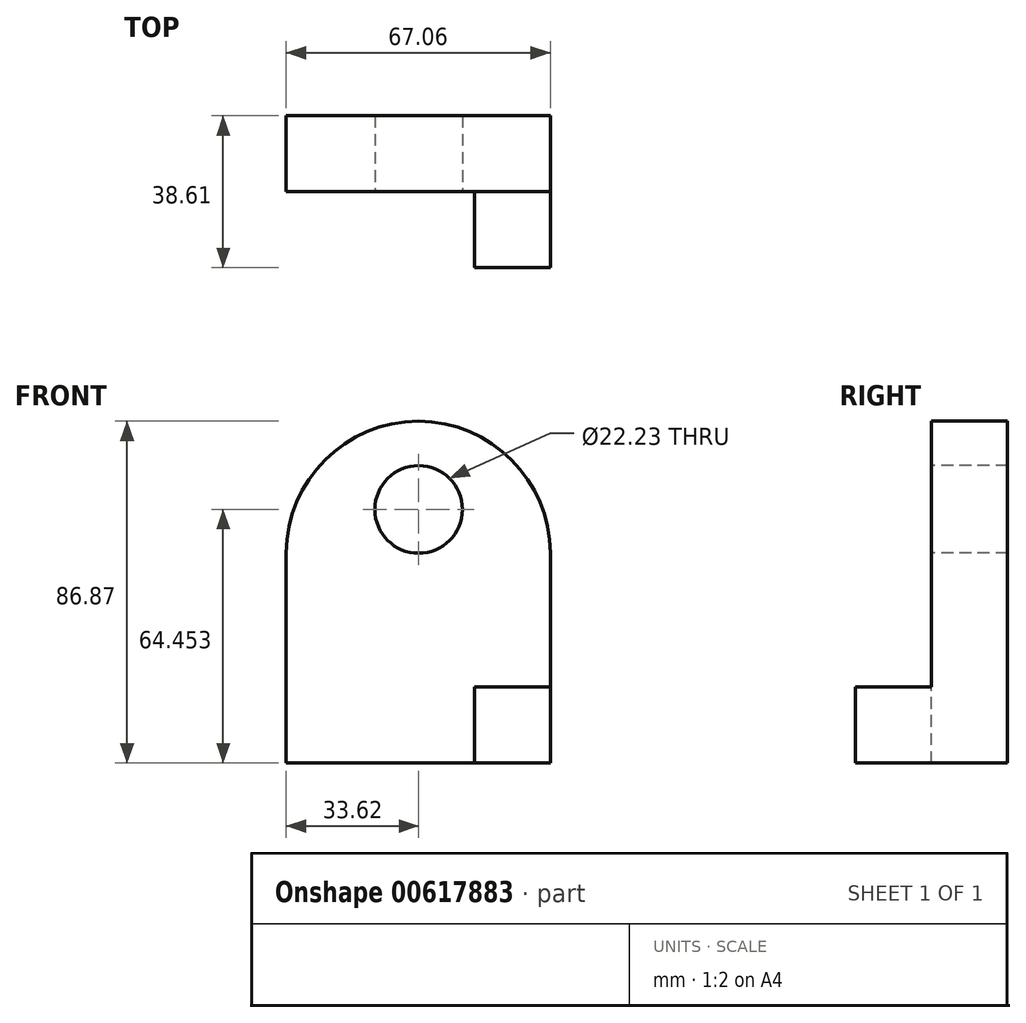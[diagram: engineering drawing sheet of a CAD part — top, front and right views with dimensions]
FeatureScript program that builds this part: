
annotation { "Feature Type Name" : "Feature", "Feature Type Description" : "" }
export const myFeature = defineFeature(function(context is Context, id is Id, definition is map)
    precondition{}
    {
        {
            var Q0;
            Q0=qCreatedBy(makeId("Front.planeOp"),FACE);
            var sketch = newSketch(context, id + "F0", { "sketchPlane" : qUnion([Q0])});
            skLineSegment(sketch, "E0", {"start": v(0, 0) * mm, "end": v(0, 53.34) * mm});
            skLineSegment(sketch, "E1", {"start": v(0, 0) * mm, "end": v(-67.06, 0) * mm});
            skLineSegment(sketch, "E2", {"start": v(-67.06, 0) * mm, "end": v(-67.06, 53.34) * mm});
            skArc(sketch, "E3", {"start": v(-67.06, 53.34) * mm, "mid": v(-33.53, 86.87) * mm, "end": v(0, 53.34) * mm});
            skSolve(sketch);
        }
        {
            var Q0;
            Q0 = qSketchRegion(id + "F0", true);
            extrude(context, id + "F1", {"entities" : qUnion([Q0]), "depth" : 19.3 * mm, "offsetDistance" : 25.4 * mm});
        }
        {
            var Q0;
            Q0=makeQuery(id+"F1.opExtrude","CAP_FACE",FACE,{"disambiguationData":[OSD([sQuery(id+"F0.wireOp",EDGE,"E0"),sQuery(id+"F0.wireOp",EDGE,"E1"),sQuery(id+"F0.wireOp",EDGE,"E2"),sQuery(id+"F0.wireOp",EDGE,"E3")])],"isStart":false});
            var sketch = newSketch(context, id + "F2", { "sketchPlane" : qUnion([Q0])});
            skSolve(sketch);
        }
        {
            var Q0;
            Q0 = qSketchRegion(id + "F0", true);
            extrude(context, id + "F3", {"entities" : qUnion([Q0]), "operationType" : NewBodyOperationType.ADD, "depth" : 19.3 * mm, "offsetDistance" : 25.4 * mm});
        }
        {
            var Q0;
            Q0=makeQuery(id+"F2.imprint","IMPRINT",FACE,{"disambiguationData":[TD([[makeQuery(id+"F2.imprint","IMPRINT",EDGE,{"derivedFrom":makeQuery(id+"F1.opExtrude","CAP_EDGE",EDGE,{"disambiguationData":[OSD([sQuery(id+"F0.wireOp",EDGE,"E0")])],"isStart":false})}),1.0]])]});
            var sketch = newSketch(context, id + "F4", { "sketchPlane" : qUnion([Q0])});
            skCircle(sketch, "E4", {"center": v(-33.44, 64.45) * mm, "radius": 11.11 * mm});
            skSolve(sketch);
        }
        {
            var Q0;
            Q0 = qSketchRegion(id + "F4", true);
            extrude(context, id + "F5", {"entities" : qUnion([Q0]), "operationType" : NewBodyOperationType.REMOVE, "oppositeDirection" : true, "depth" : 19.3 * mm, "offsetDistance" : 25.4 * mm});
        }
        {
            var Q0;
            Q0=makeQuery(id+"F2.imprint","IMPRINT",FACE,{"disambiguationData":[TD([[makeQuery(id+"F2.imprint","IMPRINT",EDGE,{"derivedFrom":makeQuery(id+"F1.opExtrude","CAP_EDGE",EDGE,{"disambiguationData":[OSD([sQuery(id+"F0.wireOp",EDGE,"E0")])],"isStart":false})}),1.0]])]});
            var sketch = newSketch(context, id + "F6", { "sketchPlane" : qUnion([Q0])});
            skLineSegment(sketch, "E5", {"start": v(0, 0) * mm, "end": v(-19.3, 0) * mm});
            skLineSegment(sketch, "E6", {"start": v(-19.3, 0) * mm, "end": v(-19.3, 19.3) * mm});
            skLineSegment(sketch, "E7", {"start": v(-19.3, 19.3) * mm, "end": v(0, 19.3) * mm});
            skLineSegment(sketch, "E8", {"start": v(0, 19.3) * mm, "end": v(0, 0) * mm});
            skSolve(sketch);
        }
        {
            var Q0;
            Q0 = qSketchRegion(id + "F6", true);
            extrude(context, id + "F7", {"entities" : qUnion([Q0]), "operationType" : NewBodyOperationType.ADD, "depth" : 19.3 * mm, "offsetDistance" : 25.4 * mm});
        }
    });
